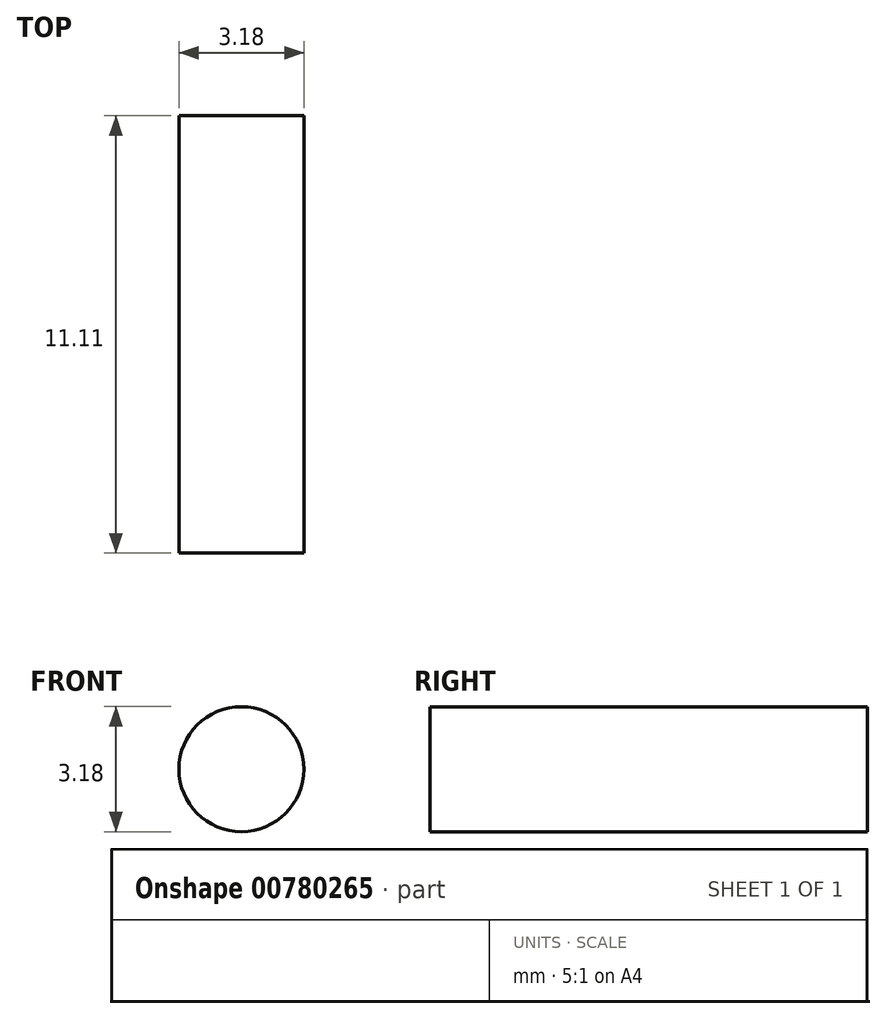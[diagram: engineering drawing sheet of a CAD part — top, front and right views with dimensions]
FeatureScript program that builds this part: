
annotation { "Feature Type Name" : "Feature", "Feature Type Description" : "" }
export const myFeature = defineFeature(function(context is Context, id is Id, definition is map)
    precondition{}
    {
        {
            var Q0;
            Q0=qCreatedBy(makeId("Front.planeOp"),FACE);
            var sketch = newSketch(context, id + "F0", { "sketchPlane" : qUnion([Q0])});
            skCircle(sketch, "E0", {"center": v(-227.48, -76.72) * mm, "radius": 1.59 * mm});
            skSolve(sketch);
        }
        {
            var Q0;
            Q0 = qSketchRegion(id + "F0", true);
            extrude(context, id + "F1", {"entities" : qUnion([Q0]), "depth" : 11.1 * mm, "offsetDistance" : 25 * mm});
        }
    });
